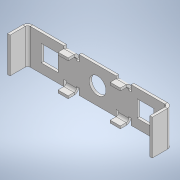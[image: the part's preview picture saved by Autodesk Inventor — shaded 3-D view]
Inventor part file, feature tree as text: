
AUTODESK INVENTOR PART (.ipt)
format: ipt  version: 2021 (Build 250183000, 183)  size: 254,464 bytes
history: native  units: mm
features: other x10, sketch x9, hole x4, sheet_metal_op x3, mirror x2
ambient origin geometry x8: Origin, YZ Plane, XZ Plane, XY Plane, X Axis, Y Axis, Z Axis, Center Point
bodies: Body1 (feature_tree)
feature tree (28):
  other  "Sólido1"
  sheet_metal_op  "Face1"
  sheet_metal_op  "Flange1"
  sheet_metal_op  "Flange2"
  mirror  "Espelhamento1"
  mirror  "Espelhamento2"
  hole  "Furo1"  [1 undecoded]
  hole  "Furo2"  [1 undecoded]
  hole  "Furo3"  [1 undecoded]
  hole  "Furo4"  [1 undecoded]
  sketch  "Esboço1"  dims[d0=172.0mm d1=42.0mm]
  other  "Placa1"
  sketch  "Esboço2"  dims[d2=3.0mm d3=3.0mm]
  other  "Placa2"
  other  "Vergadura1"
  other  "Canto1"
  sketch  "Esboço3"  dims[d4=1.5mm d5=6.0mm]
  sketch  "Esboço4"  dims[d6=3.0mm d7=21.0mm d8=90.0deg d9=3.0mm]
  other  "Placa3"
  other  "Vergadura2"
  other  "Canto2"
  sketch  "Esboço5"  dims[d10=12.0mm]
  sketch  "Esboço6"  dims[d11=3.0mm]
  sketch  "Esboço7"  dims[d12=3.0mm]
  sketch  "Esboço8"  dims[d13=180.0deg]
  sketch  "Esboço9"  dims[d15=18.0mm d16=3.0mm d17=3.0mm d18=0.0mm d19=3.0mm d20=1.5mm d21=6.0mm d22=3.0mm d23=10.0mm d24=90.0deg d25=3.0mm d26=12.0mm d27=3.0mm d28=3.0mm d29=14.0mm d30=20.0mm d31=3.0mm d32=0.0mm d33=5.0mm d34=20.0mm d35=6.0mm d36=4.0mm d37=2.0mm d38=90.0deg d39=3.0mm d40=20.594885mm d41=3.5mm d42=6.0mm d43=2.459mm d44=42.0mm d45=4.0mm d46=2.0mm d47=90.0deg d48=3.0mm d49=0.0mm d50=3.5mm d51=6.0mm d52=2.459mm d53=42.0mm d54=4.0mm d55=2.0mm d56=90.0deg d57=3.0mm d58=0.0mm d59=2.459mm d60=300.0mm d61=4.0mm d62=2.0mm d63=90.0deg d64=3.0mm d65=0.0mm]
  other  "Recortar1"
  other  "Recortar2"
note: 4 required parameter values undecoded (feature->parameter linkage not recoverable at this tier; creation-order binding heuristic only, values carry confidence <= 0.55)
